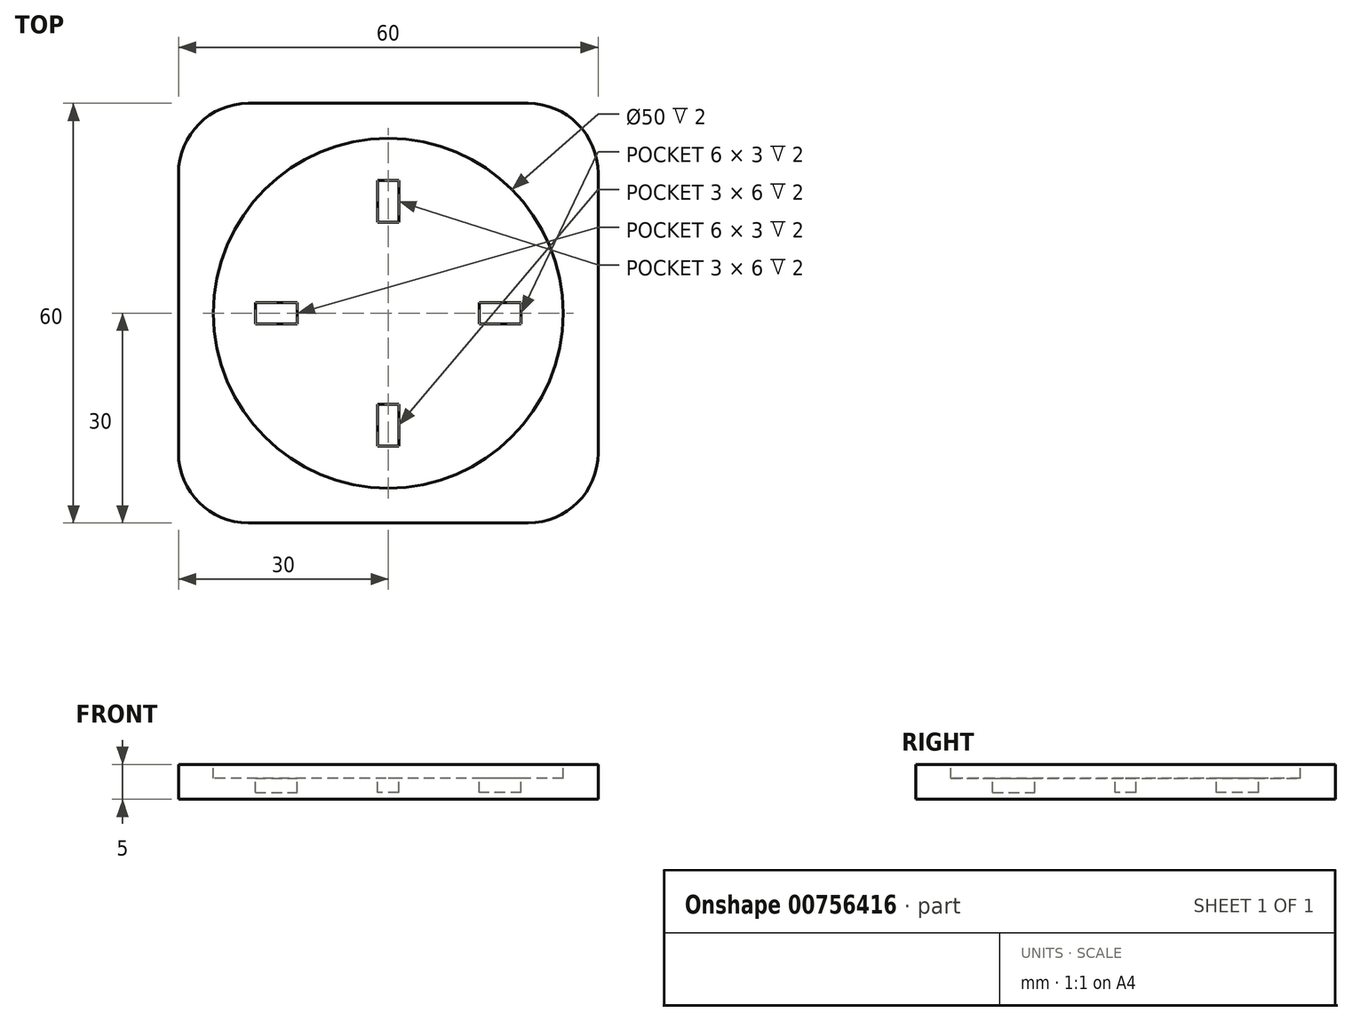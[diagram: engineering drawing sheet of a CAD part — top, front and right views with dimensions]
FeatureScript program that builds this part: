
annotation { "Feature Type Name" : "Feature", "Feature Type Description" : "" }
export const myFeature = defineFeature(function(context is Context, id is Id, definition is map)
    precondition{}
    {
        {
            var Q0;
            Q0=qCreatedBy(makeId("Top.planeOp"),FACE);
            var sketch = newSketch(context, id + "F0", { "sketchPlane" : qUnion([Q0])});
            skLineSegment(sketch, "E0.bottom", {"start": v(30, 30) * mm, "end": v(-30, 30) * mm});
            skLineSegment(sketch, "E0.top", {"start": v(30, -30) * mm, "end": v(-30, -30) * mm});
            skLineSegment(sketch, "E0.left", {"start": v(30, 30) * mm, "end": v(30, -30) * mm});
            skLineSegment(sketch, "E0.right", {"start": v(-30, 30) * mm, "end": v(-30, -30) * mm});
            skPoint(sketch, "E0.middle", {"position": v(0, 0) * mm});
            skSolve(sketch);
        }
        {
            var Q0;
            Q0 = qSketchRegion(id + "F0", true);
            extrude(context, id + "F1", {"entities" : qUnion([Q0]), "depth" : 5 * mm, "offsetDistance" : 25 * mm});
        }
        {
            var Q0;
            Q0=makeQuery(id+"F1.opExtrude","CAP_FACE",FACE,{"disambiguationData":[OSD([sQuery(id+"F0.wireOp",EDGE,"E0.bottom"),sQuery(id+"F0.wireOp",EDGE,"E0.top"),sQuery(id+"F0.wireOp",EDGE,"E0.left"),sQuery(id+"F0.wireOp",EDGE,"E0.right")])],"isStart":false});
            var sketch = newSketch(context, id + "F2", { "sketchPlane" : qUnion([Q0])});
            skCircle(sketch, "E1", {"center": v(0, 0) * mm, "radius": 25 * mm});
            skSolve(sketch);
        }
        {
            var Q0;
            Q0 = qSketchRegion(id + "F2", true);
            extrude(context, id + "F3", {"entities" : qUnion([Q0]), "operationType" : NewBodyOperationType.ADD, "oppositeDirection" : true, "depth" : 2 * mm, "offsetDistance" : 25 * mm});
        }
        {
            var Q0;
            Q0=makeQuery(id+"F1.opExtrude","CAP_FACE",FACE,{"disambiguationData":[OSD([sQuery(id+"F0.wireOp",EDGE,"E0.bottom"),sQuery(id+"F0.wireOp",EDGE,"E0.top"),sQuery(id+"F0.wireOp",EDGE,"E0.left"),sQuery(id+"F0.wireOp",EDGE,"E0.right")])],"isStart":false});
            var sketch = newSketch(context, id + "F4", { "sketchPlane" : qUnion([Q0])});
            skCircle(sketch, "E2", {"center": v(0, 0) * mm, "radius": 25 * mm});
            skSolve(sketch);
        }
        {
            var Q0;
            Q0=makeQuery(id+"F4.imprint","IMPRINT",FACE,{"disambiguationData":[TD([[makeQuery(id+"F4.imprint","IMPRINT",EDGE,{"derivedFrom":sQuery(id+"F4.wireOp",EDGE,"E2")}),1.0]])]});
            extrude(context, id + "F5", {"entities" : qUnion([Q0]), "operationType" : NewBodyOperationType.REMOVE, "oppositeDirection" : true, "depth" : 2 * mm, "offsetDistance" : 25 * mm});
        }
        {
            var Q0;
            Q0=makeQuery(id+"F1.opExtrude","SWEPT_EDGE",EDGE,{"disambiguationData":[OSD([sQuery(id+"F0.wireOp",EDGE,"E0.top"),sQuery(id+"F0.wireOp",EDGE,"E0.right")])]});
            var Q1;
            Q1=makeQuery(id+"F1.opExtrude","SWEPT_EDGE",EDGE,{"disambiguationData":[OSD([sQuery(id+"F0.wireOp",EDGE,"E0.bottom"),sQuery(id+"F0.wireOp",EDGE,"E0.right")])]});
            var Q2;
            Q2=makeQuery(id+"F1.opExtrude","SWEPT_EDGE",EDGE,{"disambiguationData":[OSD([sQuery(id+"F0.wireOp",EDGE,"E0.bottom"),sQuery(id+"F0.wireOp",EDGE,"E0.left")])]});
            var Q3;
            Q3=makeQuery(id+"F1.opExtrude","SWEPT_EDGE",EDGE,{"disambiguationData":[OSD([sQuery(id+"F0.wireOp",EDGE,"E0.top"),sQuery(id+"F0.wireOp",EDGE,"E0.left")])]});
            fillet(context, id + "F6", {"entities" : qUnion([Q0, Q1, Q2, Q3]), "radius" : 10 * mm, "tangentPropagation" : true, "allowEdgeOverflow" : false});
        }
        {
            var Q0;
            Q0=makeQuery(id+"F5.boolean.opBoolean","COPY",FACE,{"derivedFrom":makeQuery(id+"F5.opExtrude","CAP_FACE",FACE,{"disambiguationData":[OSD([sQuery(id+"F4.wireOp",EDGE,"E2")])],"isStart":false})});
            var sketch = newSketch(context, id + "F7", { "sketchPlane" : qUnion([Q0])});
            skLineSegment(sketch, "E3.bottom", {"start": v(-1.5, 19) * mm, "end": v(1.5, 19) * mm});
            skLineSegment(sketch, "E3.top", {"start": v(-1.5, 13) * mm, "end": v(1.5, 13) * mm});
            skLineSegment(sketch, "E3.left", {"start": v(-1.5, 19) * mm, "end": v(-1.5, 13) * mm});
            skLineSegment(sketch, "E3.right", {"start": v(1.5, 19) * mm, "end": v(1.5, 13) * mm});
            skPoint(sketch, "E3.middle", {"position": v(0, 16) * mm});
            skLineSegment(sketch, "E4.1.0", {"start": v(-19, -1.5) * mm, "end": v(-13, -1.5) * mm});
            skLineSegment(sketch, "E4.1.1", {"start": v(-19, -1.5) * mm, "end": v(-19, 1.5) * mm});
            skLineSegment(sketch, "E4.1.2", {"start": v(-19, 1.5) * mm, "end": v(-13, 1.5) * mm});
            skLineSegment(sketch, "E4.1.3", {"start": v(-13, -1.5) * mm, "end": v(-13, 1.5) * mm});
            skLineSegment(sketch, "E4.2.0", {"start": v(1.5, -19) * mm, "end": v(1.5, -13) * mm});
            skLineSegment(sketch, "E4.2.1", {"start": v(1.5, -19) * mm, "end": v(-1.5, -19) * mm});
            skLineSegment(sketch, "E4.2.2", {"start": v(-1.5, -19) * mm, "end": v(-1.5, -13) * mm});
            skLineSegment(sketch, "E4.2.3", {"start": v(1.5, -13) * mm, "end": v(-1.5, -13) * mm});
            skLineSegment(sketch, "E4.3.0", {"start": v(19, 1.5) * mm, "end": v(13, 1.5) * mm});
            skLineSegment(sketch, "E4.3.1", {"start": v(19, 1.5) * mm, "end": v(19, -1.5) * mm});
            skLineSegment(sketch, "E4.3.2", {"start": v(19, -1.5) * mm, "end": v(13, -1.5) * mm});
            skLineSegment(sketch, "E4.3.3", {"start": v(13, 1.5) * mm, "end": v(13, -1.5) * mm});
            skPoint(sketch, "E4.center", {"position": v(0, 0) * mm});
            skSolve(sketch);
        }
        {
            var Q0;
            Q0=makeQuery(id+"F7.imprint","IMPRINT",FACE,{"disambiguationData":[TD([[makeQuery(id+"F7.imprint","IMPRINT",EDGE,{"derivedFrom":sQuery(id+"F7.wireOp",EDGE,"E3.bottom")}),-1.0]])]});
            var Q1;
            Q1=makeQuery(id+"F7.imprint","IMPRINT",FACE,{"disambiguationData":[TD([[makeQuery(id+"F7.imprint","IMPRINT",EDGE,{"derivedFrom":sQuery(id+"F7.wireOp",EDGE,"E4.1.0")}),1.0]])]});
            var Q2;
            Q2=makeQuery(id+"F7.imprint","IMPRINT",FACE,{"disambiguationData":[TD([[makeQuery(id+"F7.imprint","IMPRINT",EDGE,{"derivedFrom":sQuery(id+"F7.wireOp",EDGE,"E4.2.0")}),1.0]])]});
            var Q3;
            Q3=makeQuery(id+"F7.imprint","IMPRINT",FACE,{"disambiguationData":[TD([[makeQuery(id+"F7.imprint","IMPRINT",EDGE,{"derivedFrom":sQuery(id+"F7.wireOp",EDGE,"E4.3.0")}),1.0]])]});
            extrude(context, id + "F8", {"entities" : qUnion([Q0, Q1, Q2, Q3]), "operationType" : NewBodyOperationType.REMOVE, "oppositeDirection" : true, "depth" : 2 * mm, "offsetDistance" : 25 * mm});
        }
    });
